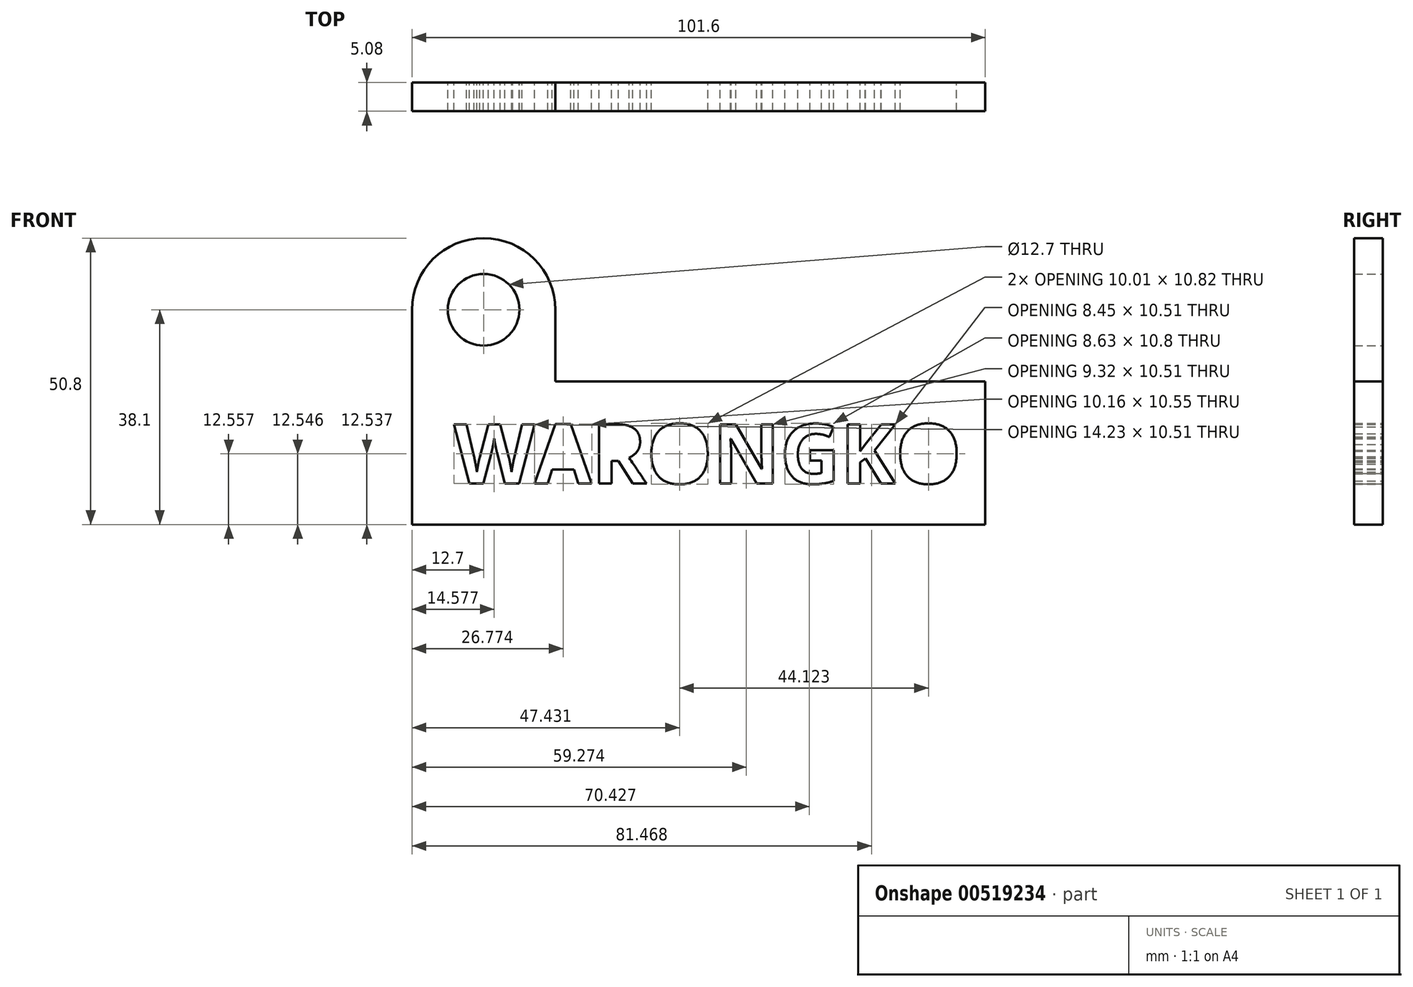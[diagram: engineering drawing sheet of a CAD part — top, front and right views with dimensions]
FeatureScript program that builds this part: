
annotation { "Feature Type Name" : "Feature", "Feature Type Description" : "" }
export const myFeature = defineFeature(function(context is Context, id is Id, definition is map)
    precondition{}
    {
        {
            var Q0;
            Q0=qCreatedBy(makeId("Front.planeOp"),FACE);
            var sketch = newSketch(context, id + "F0", { "sketchPlane" : qUnion([Q0])});
            skLineSegment(sketch, "E0.top", {"start": v(0, 0) * mm, "end": v(12.7, 0) * mm});
            skLineSegment(sketch, "E0.left", {"start": v(0, 38.1) * mm, "end": v(0, 0) * mm});
            skLineSegment(sketch, "E0.right", {"start": v(25.4, 38.1) * mm, "end": v(25.4, 25.4) * mm});
            skLineSegment(sketch, "E1.bottom", {"start": v(25.4, 25.4) * mm, "end": v(101.6, 25.4) * mm});
            skLineSegment(sketch, "E1.top", {"start": v(50.8, 0) * mm, "end": v(101.6, 0) * mm});
            skLineSegment(sketch, "E1.right", {"start": v(101.6, 25.4) * mm, "end": v(101.6, 0) * mm});
            skPoint(sketch, "E2.firstSnap0", {"position": v(101.6, 12.7) * mm});
            skPoint(sketch, "E2.firstSnap1", {"position": v(12.7, 0) * mm});
            skPoint(sketch, "E3.orphan", {"position": v(25.4, 0) * mm});
            skLineSegment(sketch, "E4", {"start": v(0, 0) * mm, "end": v(50.8, 0) * mm});
            skCircle(sketch, "E5", {"center": v(12.7, 38.1) * mm, "radius": 12.7 * mm});
            skPoint(sketch, "E5.centerSnap0", {"position": v(25.4, 38.1) * mm});
            skPoint(sketch, "E5.centerSnap1", {"position": v(12.7, 50.8) * mm});
            skPoint(sketch, "E6.orphan", {"position": v(0, 50.8) * mm});
            skPoint(sketch, "E7.orphan", {"position": v(25.4, 50.8) * mm});
            skCircle(sketch, "E8", {"center": v(12.7, 38.1) * mm, "radius": 6.35 * mm});
            skText(sketch, "E9", { "text": "WARONGKO", "fontName": "OpenSans-Bold.ttf"});
            const initialGuessF0  = {"E9": [0.00746, 0.00728, 1, 0, 0.0106]};
            skSetInitialGuess(sketch, initialGuessF0);
            skSolve(sketch);
        }
        {
            var Q0;
            Q0=makeQuery(id+"F0.imprint","IMPRINT",FACE,{"disambiguationData":[TD([[makeQuery(id+"F0.imprint","IMPRINT",EDGE,{"derivedFrom":sQuery(id+"F0.wireOp",EDGE,"E0.bottom")}),-1.0]])]});
            var Q1;
            {var subQ0=sQuery(id+"F0.wireOp",EDGE,"E5");var subQ1=makeQuery(id+"F0.imprint","INTERSECT",VERTEX,{"derivedFrom":[sQuery(id+"F0.wireOp",EDGE,"E0.left"),subQ0]});Q1=makeQuery(id+"F0.imprint","IMPRINT",FACE,{"disambiguationData":[TD([[makeQuery(id+"F0.imprint","IMPRINT",EDGE,{"disambiguationData":[TD([[subQ1,1.0]])],"derivedFrom":subQ0}),1.0]])]});}
            var Q2;
            {var subQ2=sQuery(id+"F0.wireOp",EDGE,"E0.left");Q2=makeQuery(id+"F0.imprint","IMPRINT",FACE,{"disambiguationData":[TD([[makeQuery(id+"F0.imprint","IMPRINT",EDGE,{"derivedFrom":subQ2}),1.0]])]});}
            extrude(context, id + "F1", {"entities" : qUnion([Q0, Q1, Q2]), "depth" : 5.08 * mm, "offsetDistance" : 25.4 * mm});
        }
        {
            var Q0;
            Q0 = qSketchRegion(id + "F0", true);
            extrude(context, id + "F2", {"entities" : qUnion([Q0]), "operationType" : NewBodyOperationType.REMOVE, "oppositeDirection" : true, "depth" : 25.4 * mm, "offsetDistance" : 25.4 * mm});
        }
    });
